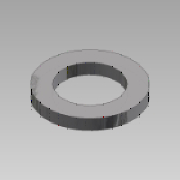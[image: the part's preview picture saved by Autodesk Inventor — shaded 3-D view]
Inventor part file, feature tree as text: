
AUTODESK INVENTOR PART (.ipt)
format: ipt  version: 2013 SP2 (Build 170200200, 200)  size: 93,696 bytes
history: native  units: mm
features: extrude x1, sketch x1
ambient origin geometry x8: Origin, YZ Plane, XZ Plane, XY Plane, X Axis, Y Axis, Z Axis, Center Point
bodies: Solid1 (feature_tree)
feature tree (2):
  extrude  "Extrusion1"  Depth=8.0mm
  sketch  "Sketch1"  dims[d0=5.0mm d1=8.0mm d2=1.0mm d3=0.0mm]
